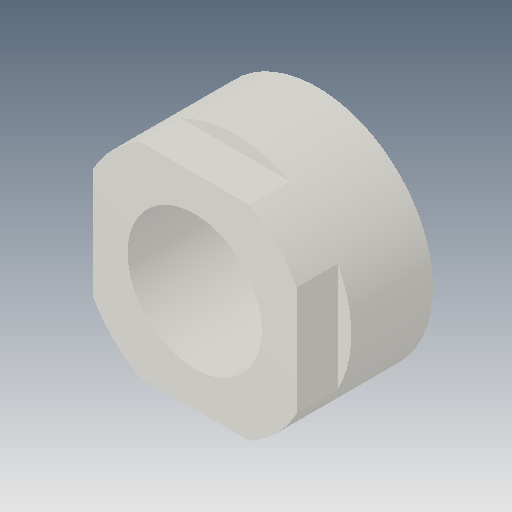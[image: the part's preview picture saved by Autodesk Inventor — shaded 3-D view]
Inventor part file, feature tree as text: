
AUTODESK INVENTOR PART (.ipt)
format: ipt  version: 2018 (Build 220112000, 112)  size: 112,640 bytes
history: native  units: mm
features: extrude x2, sketch x2
ambient origin geometry x8: Origin, YZ Plane, XZ Plane, XY Plane, X Axis, Y Axis, Z Axis, Center Point
bodies: Solid1 (feature_tree)
feature tree (4):
  extrude  "Extrusion1"  Depth=17.0mm
  extrude  "Extrusion2"  Depth=15.0mm
  sketch  "Sketch1"  dims[d0=9.8602mm d1=17.0mm]
  sketch  "Sketch2"  dims[d2=9.0mm d3=0.0mm d4=15.0mm d5=3.0mm d6=0.0mm]
